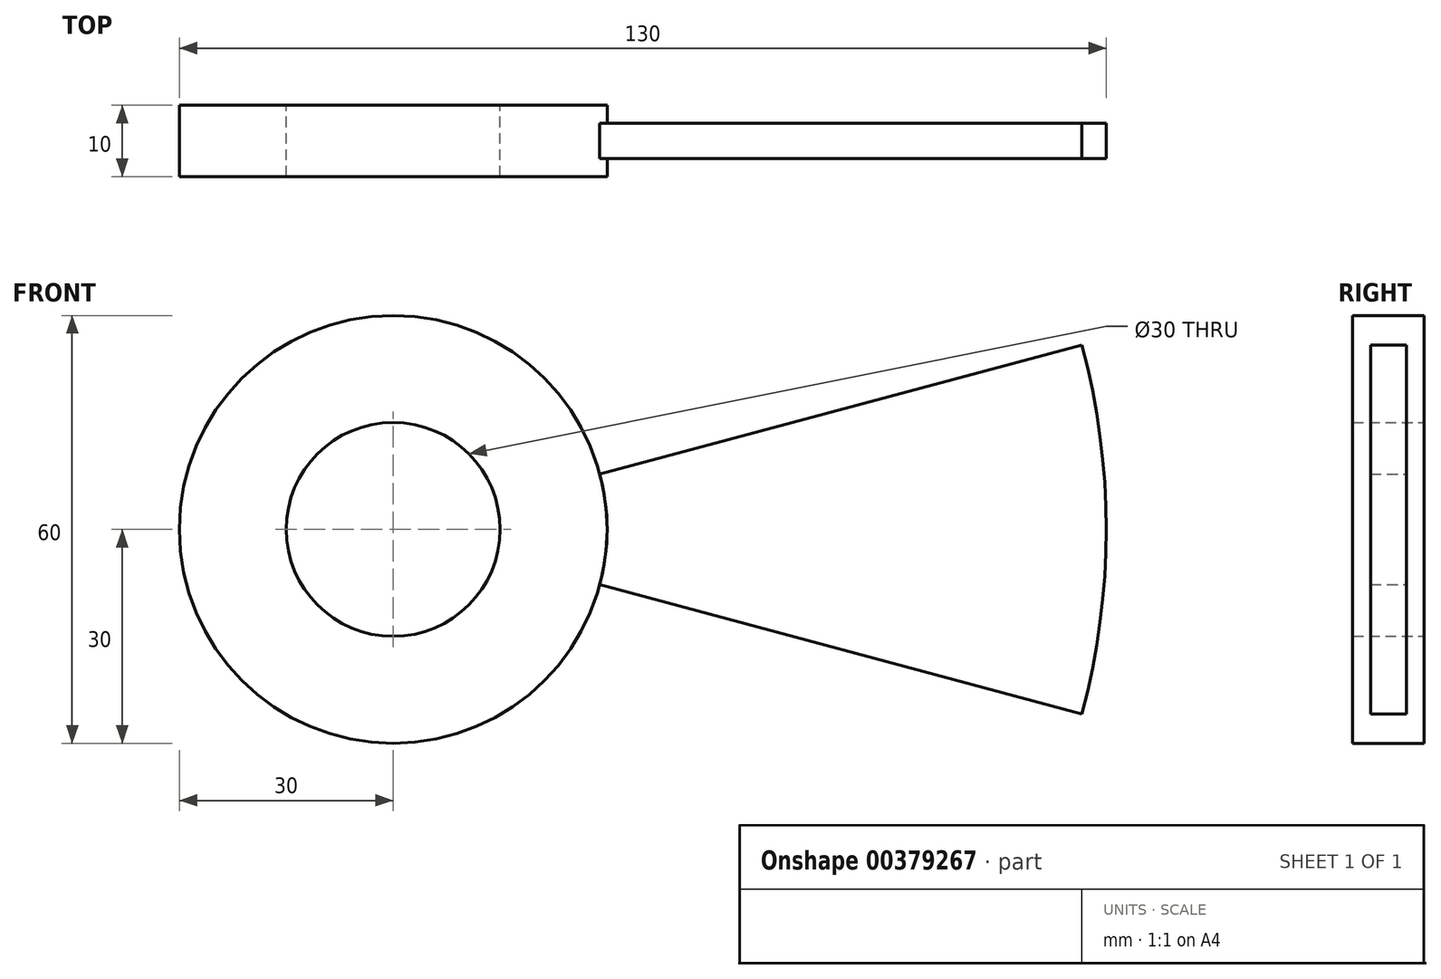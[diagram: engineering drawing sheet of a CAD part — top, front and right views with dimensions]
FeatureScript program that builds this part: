
annotation { "Feature Type Name" : "Feature", "Feature Type Description" : "" }
export const myFeature = defineFeature(function(context is Context, id is Id, definition is map)
    precondition{}
    {
        {
            var Q0;
            Q0=qCreatedBy(makeId("Front.planeOp"),FACE);
            var sketch = newSketch(context, id + "F0", { "sketchPlane" : qUnion([Q0])});
            skCircle(sketch, "E0", {"center": v(0, 0) * mm, "radius": 30 * mm});
            skCircle(sketch, "E1", {"center": v(0, 0) * mm, "radius": 15 * mm});
            skSolve(sketch);
        }
        {
            var Q0;
            Q0=makeQuery(id+"F0.imprint","IMPRINT",FACE,{"disambiguationData":[TD([[makeQuery(id+"F0.imprint","IMPRINT",EDGE,{"derivedFrom":sQuery(id+"F0.wireOp",EDGE,"E0")}),1.0]])]});
            extrude(context, id + "F1", {"entities" : qUnion([Q0]), "depth" : 10 * mm});
        }
        {
            var Q0;
            Q0=qCreatedBy(makeId("Front.planeOp"),FACE);
            cPlane(context, id + "F2", {"entities" : qUnion([Q0]), "cplaneType" : CPlaneType.OFFSET, "offset" : 5 * mm, "width" : 150 * mm, "height" : 150 * mm});
        }
        {
            var Q0;
            Q0=qCreatedBy(id+"F2.planeOp",FACE);
            var sketch = newSketch(context, id + "F3", { "sketchPlane" : qUnion([Q0])});
            skLineSegment(sketch, "E2", {"start": v(0, 0) * mm, "end": v(14.49, 3.88) * mm, "construction": true});
            skLineSegment(sketch, "E3", {"start": v(96.6, -25.88) * mm, "end": v(14.49, -3.88) * mm});
            skArc(sketch, "E4", {"start": v(96.6, -25.88) * mm, "mid": v(100, 0) * mm, "end": v(96.6, 25.88) * mm});
            skArc(sketch, "E5", {"start": v(14.49, 3.88) * mm, "mid": v(-15, 0) * mm, "end": v(14.49, -3.88) * mm});
            skArc(sketch, "E6", {"start": v(14.49, -3.88) * mm, "mid": v(15, 0) * mm, "end": v(14.49, 3.88) * mm});
            skLineSegment(sketch, "E7", {"start": v(14.49, 3.88) * mm, "end": v(96.6, 25.88) * mm});
            skLineSegment(sketch, "E8", {"start": v(14.49, -3.88) * mm, "end": v(0, 0) * mm, "construction": true});
            skLineSegment(sketch, "E9", {"start": v(14.49, -3.88) * mm, "end": v(96.6, -25.88) * mm});
            skArc(sketch, "E10", {"start": v(28.98, 7.76) * mm, "mid": v(30, 0) * mm, "end": v(28.98, -7.76) * mm});
            skSolve(sketch);
        }
        {
            var Q0;
            {var subQ0=sQuery(id+"F3.wireOp",EDGE,"E4");Q0=makeQuery(id+"F3.imprint","IMPRINT",FACE,{"disambiguationData":[TD([[makeQuery(id+"F3.imprint","IMPRINT",EDGE,{"derivedFrom":subQ0}),1.0]])]});}
            extrude(context, id + "F4", {"entities" : qUnion([Q0]), "operationType" : NewBodyOperationType.ADD, "endBound" : BoundingType.SYMMETRIC, "depth" : 5 * mm});
        }
    });
